# Revit family: LEGRAND_TOMAS SIN ENCLAVAMIENTO_DE SUPERFICIE_IP66_400
name_source: partatom
category: Installations électriques
revit_build: Autodesk Revit 2018 (Build: 20170223_1515(x64)
units: mm (PartAtom-declared; Revit-internal decimal feet)

## family parameters
Conserver l'orientation des annotations = Non
Cote de connecteur circulaire = Utiliser le diamètre
Couper avec des vides une fois chargée = Non
Hôte = Face
Partagée = Non
Point de calcul de pièce = Non
Type d'élément = Normal

## types (10) — shared parameters
Condiciones Generales de Uso = https://export.legrand.com
Description = Toma AL estándar internacional para montaje empotrado o en superficie con accesorio permite la alimentación de aparatos de potencia
Dia bouchon = 90 mm  [stored 0.295276 ft]
Elévation par défaut = 1000 mm  [stored 3.28084 ft]
Estándar CEI o NFC = CEI
Fabricant = Legrand
L2 = 40 mm  [stored 0.131234 ft]
RAY BOUCHON = 45 mm  [stored 0.147638 ft]
Ray = 28 mm
Temperatura maxima de instalación = 40°C
Temperatura maxima de uso = 100°C
Temperatura minima de instalación = -20°C
Temperatura minima de uso = -50°C
Tension V = 400 V  50/60 Hz rojo
clase de protección IP = IP66/67-55
color característico = rojo
dIA = 56 mm
instalación de empotrar E o de superficie S = empotrar y superficie
materia de la caja = plástico
resistencia a los choques IK = 09
sin halogeno = Non
tipo de conexión = conexión por tonillo

## per-type parameters (varying)
| type | Modèle | altura mm | ancho mm | distancia de fijación horizontal mm | distancia de fijación vertical mm | h1 | intensidad A | numero de polos | posición de la tierra h | profundidad de empotrar mm | profundidad mm |
| base para cuadro Hypra   IP66/67-55   16 A   380/415 V   3P+T   plast caja de superficie para cableado de paso | 051130 | 182 mm | 86 mm | 60 mm | 70 mm | 109 mm | 16 A | 4 | 6 | 75 mm | 145 mm |
| base para cuadro Hypra   IP66/67-55   16 A   380/415 V   3P+N+T   plast caja de superficie para cableado de paso | 051131 | 182 mm | 86 mm | 60 mm | 70 mm | 109 mm | 16 A | 6 | 6 | 75 mm | 145 mm |
| base para cuadro entreejes unificados Hypra  IP66/67-55  32 A   380/415 V   3P+T   plast caja de superficie para cableado de paso | 053050 | 162 mm | 102 mm | 70 mm | 70 mm | 97 mm | 32 A | 4 | 6 | 90 mm  [stored 0.295276 ft] | 160 mm  [stored 0.524934 ft] |
| base para cuadro entreejes unificados Hypra  IP66/67 55  32 A  380/415 V   3P+N+T  plast caja de superficie para cableado de paso | 053051 | 162 mm | 102 mm | 70 mm | 70 mm | 97 mm | 32 A | 5 | 6 | 90 mm  [stored 0.295276 ft] | 160 mm  [stored 0.524934 ft] |
| base para cuadro Hypra  IP 66/67-55   63A   380/415 V   3P+T   plast caja de superficie para cableado de paso | 059427 | 300 mm | 170 mm | 77 mm | 85 mm | 180 mm  [stored 0.590551 ft] | 63 A | 4 | 9 | 150 mm | 225 mm |
| base para cuadro Hypra  IP 66/67-55   63A   380/415 V   3P+N+T   plast caja de superficie para cableado de paso | 059428 | 300 mm | 170 mm | 77 mm | 85 mm | 180 mm  [stored 0.590551 ft] | 63 A | 4 | 9 | 150 mm | 225 mm |
| base para cuadro Hypra   IP66/67-55   16 A   380/415 V   3P+T   plast montaje de superficie con caja simple | 051130 | 106 mm | 74 mm | 60 mm | 70 mm | 64 mm | 16 A | 4 | 6 | 58 mm | 115 mm |
| base para cuadro Hypra   IP66/67-55   16 A   380/415 V   3P+N+T   plast montaje de superficie con caja simple | 051131 | 106 mm | 74 mm | 60 mm | 70 mm | 64 mm | 16 A | 6 | 6 | 58 mm | 115 mm |
| base para cuadro entreejes unificados Hypra  IP66/67-55  32 A   380/415 V   3P+T   plast montaje de superficie con caja simple | 053050 | 162 mm | 102 mm | 70 mm | 70 mm | 97 mm | 32 A | 4 | 6 | 90 mm  [stored 0.295276 ft] | 160 mm  [stored 0.524934 ft] |
| base para cuadro entreejes unificados Hypra  IP66/67-55  32 A  380/415 V   3P+N+T  plast montaje de superficie con caja simple | 053051 | 162 mm | 102 mm | 70 mm | 70 mm | 97 mm | 32 A | 5 | 6 | 90 mm  [stored 0.295276 ft] | 160 mm  [stored 0.524934 ft] |

note: [stored X ft] marks values corroborated as IEEE doubles in the binary element streams (Revit-internal decimal feet)
